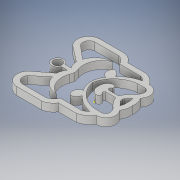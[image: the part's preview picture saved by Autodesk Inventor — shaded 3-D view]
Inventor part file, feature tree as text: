
AUTODESK INVENTOR PART (.ipt)
format: ipt  version: 2019 (Build 230136000, 136)  size: 330,240 bytes
history: native  units: mm
features: sketch x9, extrude x8
ambient origin geometry x8: Origin, YZ Plane, XZ Plane, XY Plane, X Axis, Y Axis, Z Axis, Center Point
bodies: Solid1 (feature_tree)
feature tree (17):
  extrude  "Extrusion1"  Depth=60.0mm
  extrude  "Extrusion2"  Depth=3.0mm
  extrude  "Extrusion3"  Depth=3.0mm TaperAngle=0.0deg
  extrude  "Extrusion4"  Depth=3.0mm TaperAngle=0.0deg
  extrude  "Extrusion5"  Depth=3.0mm TaperAngle=0.0deg
  extrude  "Extrusion6"  Depth=3.0mm TaperAngle=0.0deg
  sketch  "Sketch7"  dims[d45=4.5mm d46=3.0mm d47=0.0mm]
  extrude  "Extrusion7"  Depth=3.0mm TaperAngle=0.0deg
  extrude  "Extrusion8"  [1 undecoded]
  sketch  "Sketch1"  dims[d0=60.0mm d1=60.0mm]
  sketch  "Sketch2"  dims[d2=3.0mm d3=0.0mm d23=7.0mm]
  sketch  "Sketch3"  dims[d29=3.0mm d30=0.0mm d31=6.0mm d32=0.0mm]
  sketch  "Sketch4"  dims[d33=50.0mm d34=3.0mm d35=0.0mm]
  sketch  "Sketch5"  dims[d36=2.0mm d37=3.0mm d38=0.0mm]
  sketch  "Sketch6"  dims[d39=32.5mm d40=29.0mm d41=0.0mm d42=0.0mm d43=3.0mm d44=0.0mm]
  sketch  "Sketch8"  dims[d48=3.0mm d49=0.0mm]
  sketch  "Sketch9"
note: 1 required parameter value undecoded (feature->parameter linkage not recoverable at this tier; creation-order binding heuristic only, values carry confidence <= 0.55)
